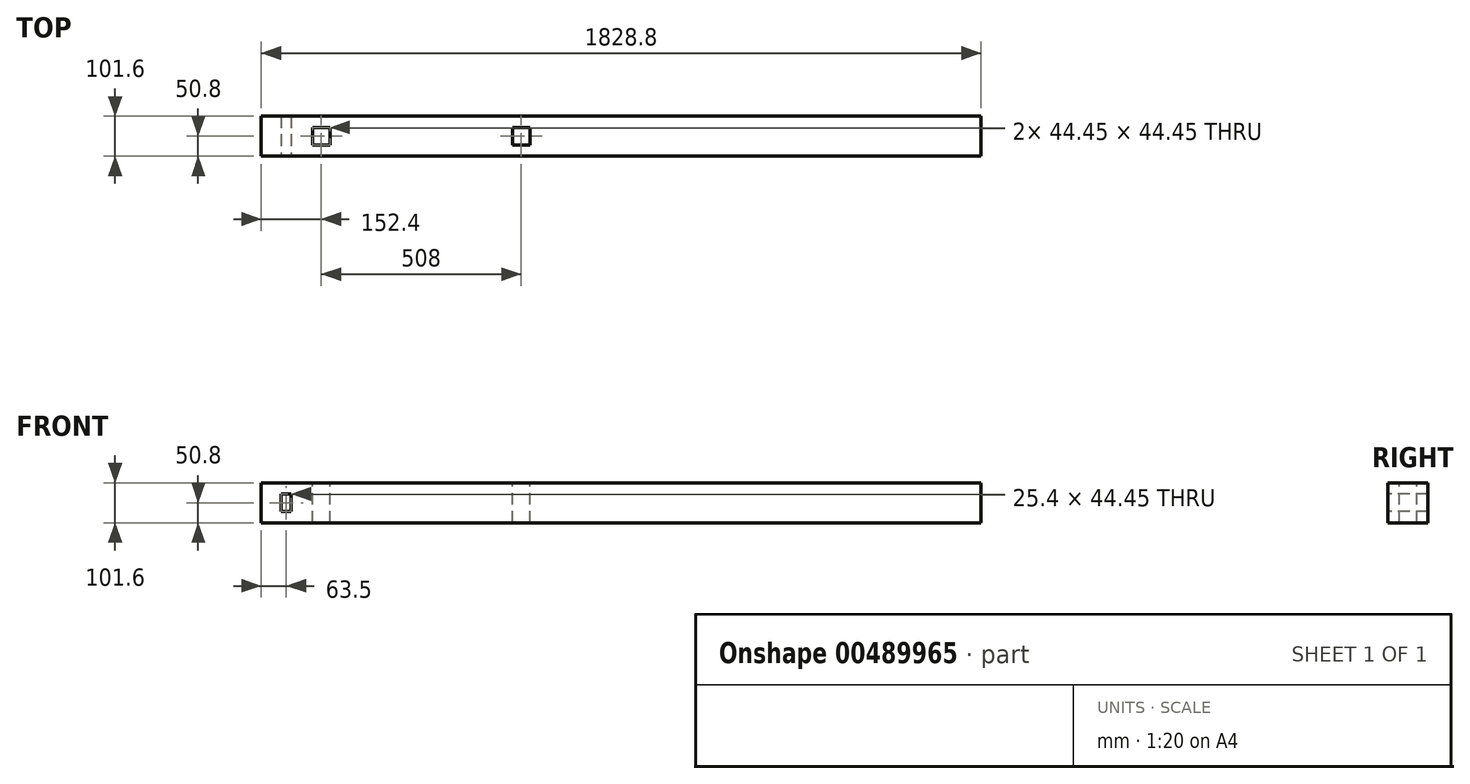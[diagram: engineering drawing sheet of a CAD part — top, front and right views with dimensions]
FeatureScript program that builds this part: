
annotation { "Feature Type Name" : "Feature", "Feature Type Description" : "" }
export const myFeature = defineFeature(function(context is Context, id is Id, definition is map)
    precondition{}
    {
        {
            var Q0;
            Q0=qCreatedBy(makeId("Right.planeOp"),FACE);
            var sketch = newSketch(context, id + "F0", { "sketchPlane" : qUnion([Q0])});
            skLineSegment(sketch, "E0.bottom", {"start": v(-50.8, 50.8) * mm, "end": v(50.8, 50.8) * mm});
            skLineSegment(sketch, "E0.top", {"start": v(-50.8, -50.8) * mm, "end": v(50.8, -50.8) * mm});
            skLineSegment(sketch, "E0.left", {"start": v(-50.8, 50.8) * mm, "end": v(-50.8, -50.8) * mm});
            skLineSegment(sketch, "E0.right", {"start": v(50.8, 50.8) * mm, "end": v(50.8, -50.8) * mm});
            skPoint(sketch, "E0.middle", {"position": v(0, 0) * mm});
            skSolve(sketch);
        }
        {
            var Q0;
            Q0=makeQuery(id+"F0.imprint","IMPRINT",FACE,{"disambiguationData":[TD([[makeQuery(id+"F0.imprint","IMPRINT",EDGE,{"derivedFrom":sQuery(id+"F0.wireOp",EDGE,"E0.bottom")}),-1.0]])]});
            extrude(context, id + "F1", {"entities" : qUnion([Q0]), "endBound" : BoundingType.SYMMETRIC, "depth" : 1828.8 * mm});
        }
        {
            var Q0;
            Q0=makeQuery(id+"F1.opExtrude","SWEPT_FACE",FACE,{"disambiguationData":[OSD([sQuery(id+"F0.wireOp",EDGE,"E0.bottom")])]});
            var sketch = newSketch(context, id + "F2", { "sketchPlane" : qUnion([Q0])});
            skLineSegment(sketch, "E1.bottom", {"start": v(-784.23, 22.22) * mm, "end": v(-739.78, 22.22) * mm});
            skLineSegment(sketch, "E1.top", {"start": v(-784.23, -22.23) * mm, "end": v(-739.78, -22.23) * mm});
            skLineSegment(sketch, "E1.left", {"start": v(-784.23, 22.22) * mm, "end": v(-784.23, -22.23) * mm});
            skLineSegment(sketch, "E1.right", {"start": v(-739.78, 22.22) * mm, "end": v(-739.78, -22.23) * mm});
            skPoint(sketch, "E1.middle", {"position": v(-762, 0) * mm});
            skSolve(sketch);
        }
        {
            var Q0;
            Q0=qSketchRegion(id+"F2",true);
            extrude(context, id + "F3", {"entities" : qUnion([Q0]), "operationType" : NewBodyOperationType.REMOVE, "endBound" : BoundingType.THROUGH_ALL, "oppositeDirection" : true, "depth" : 25.4 * mm});
        }
        {
            var Q0;
            Q0=makeQuery(id+"F1.opExtrude","SWEPT_FACE",FACE,{"disambiguationData":[OSD([sQuery(id+"F0.wireOp",EDGE,"E0.bottom")])]});
            var sketch = newSketch(context, id + "F4", { "sketchPlane" : qUnion([Q0])});
            skLineSegment(sketch, "E2.bottom", {"start": v(-276.23, 22.23) * mm, "end": v(-231.78, 22.23) * mm});
            skLineSegment(sketch, "E2.top", {"start": v(-276.23, -22.22) * mm, "end": v(-231.78, -22.22) * mm});
            skLineSegment(sketch, "E2.left", {"start": v(-276.23, 22.23) * mm, "end": v(-276.23, -22.22) * mm});
            skLineSegment(sketch, "E2.right", {"start": v(-231.78, 22.23) * mm, "end": v(-231.78, -22.22) * mm});
            skPoint(sketch, "E2.middle", {"position": v(-254, 0) * mm});
            skSolve(sketch);
        }
        {
            var Q0;
            Q0=makeQuery(id+"F4.imprint","IMPRINT",FACE,{"disambiguationData":[TD([[makeQuery(id+"F4.imprint","IMPRINT",EDGE,{"derivedFrom":sQuery(id+"F4.wireOp",EDGE,"E2.bottom")}),-1.0]])]});
            extrude(context, id + "F5", {"entities" : qUnion([Q0]), "operationType" : NewBodyOperationType.REMOVE, "endBound" : BoundingType.THROUGH_ALL, "oppositeDirection" : true, "depth" : 25.4 * mm});
        }
        {
            var Q0;
            Q0=makeQuery(id+"F1.opExtrude","SWEPT_FACE",FACE,{"disambiguationData":[OSD([sQuery(id+"F0.wireOp",EDGE,"E0.left")])]});
            var sketch = newSketch(context, id + "F6", { "sketchPlane" : qUnion([Q0])});
            skLineSegment(sketch, "E3.bottom", {"start": v(-863.6, -22.23) * mm, "end": v(-838.2, -22.23) * mm});
            skLineSegment(sketch, "E3.top", {"start": v(-863.6, 22.23) * mm, "end": v(-838.2, 22.23) * mm});
            skLineSegment(sketch, "E3.left", {"start": v(-863.6, -22.23) * mm, "end": v(-863.6, 22.23) * mm});
            skLineSegment(sketch, "E3.right", {"start": v(-838.2, -22.23) * mm, "end": v(-838.2, 22.23) * mm});
            skPoint(sketch, "E3.middle", {"position": v(-850.9, 0) * mm});
            skSolve(sketch);
        }
        {
            var Q0;
            Q0 = qSketchRegion(id + "F6", true);
            extrude(context, id + "F7", {"entities" : qUnion([Q0]), "operationType" : NewBodyOperationType.REMOVE, "endBound" : BoundingType.THROUGH_ALL, "oppositeDirection" : true, "depth" : 25.4 * mm});
        }
    });
